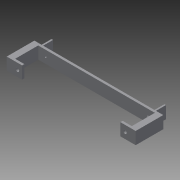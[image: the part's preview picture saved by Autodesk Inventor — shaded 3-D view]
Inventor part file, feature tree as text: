
AUTODESK INVENTOR PART (.ipt)
format: ipt  version: 2014 (Build 180170000, 170)  size: 178,688 bytes
history: native  units: mm
features: extrude x10, sketch x10, projected_geometry x3
ambient origin geometry x8: Origin, YZ Plane, XZ Plane, XY Plane, X Axis, Y Axis, Z Axis, Center Point
bodies: Solid1 (feature_tree)
feature tree (23):
  extrude  "Extrusion1"  Depth=16.0mm
  extrude  "Extrusion2"  Depth=9.0mm
  extrude  "Extrusion3"  Depth=3.0mm
  extrude  "Extrusion4"  Depth=2.5mm
  extrude  "Extrusion5"  Depth=4.0mm
  sketch  "Sketch6"  dims[d11=2.5mm d12=8.0mm d13=4.0mm d14=3.0mm d15=0.0mm]
  extrude  "Extrusion6"  Depth=3.0mm TaperAngle=0.0deg
  extrude  "Extrusion7"  Depth=3.0mm TaperAngle=0.0deg
  extrude  "Extrusion8"  Depth=8.0mm
  extrude  "Extrusion9"  Depth=20.0mm
  extrude  "Extrusion10"  Depth=3.0mm TaperAngle=0.0deg
  sketch  "Sketch1"  dims[d0=150.0mm d1=16.0mm]
  sketch  "Sketch2"  dims[d2=9.0mm d3=9.0mm]
  sketch  "Sketch3"  dims[d4=3.0mm d5=0.0mm d6=141.0mm]
  projected_geometry  "Projected Loop1"
  sketch  "Sketch4"  dims[d7=9.0mm d8=2.5mm]
  sketch  "Sketch5"  dims[d9=8.0mm d10=4.0mm]
  sketch  "Sketch7"  dims[d16=3.0mm d17=0.0mm d18=3.0mm d19=0.0mm]
  sketch  "Sketch8"  dims[d20=8.0mm d21=8.0mm]
  projected_geometry  "Projected Loop2"
  sketch  "Sketch9"  dims[d22=30.0mm d23=0.0mm d24=20.0mm]
  projected_geometry  "Projected Loop3"
  sketch  "Sketch11"  dims[d25=20.0mm d26=3.0mm d27=0.0mm d28=3.0mm d29=0.0mm d30=4.5mm d31=3.0mm d32=0.0mm d33=4.5mm d34=3.0mm d35=0.0mm d38=2.0mm d39=2.0mm d40=13.0mm d41=0.0mm]
